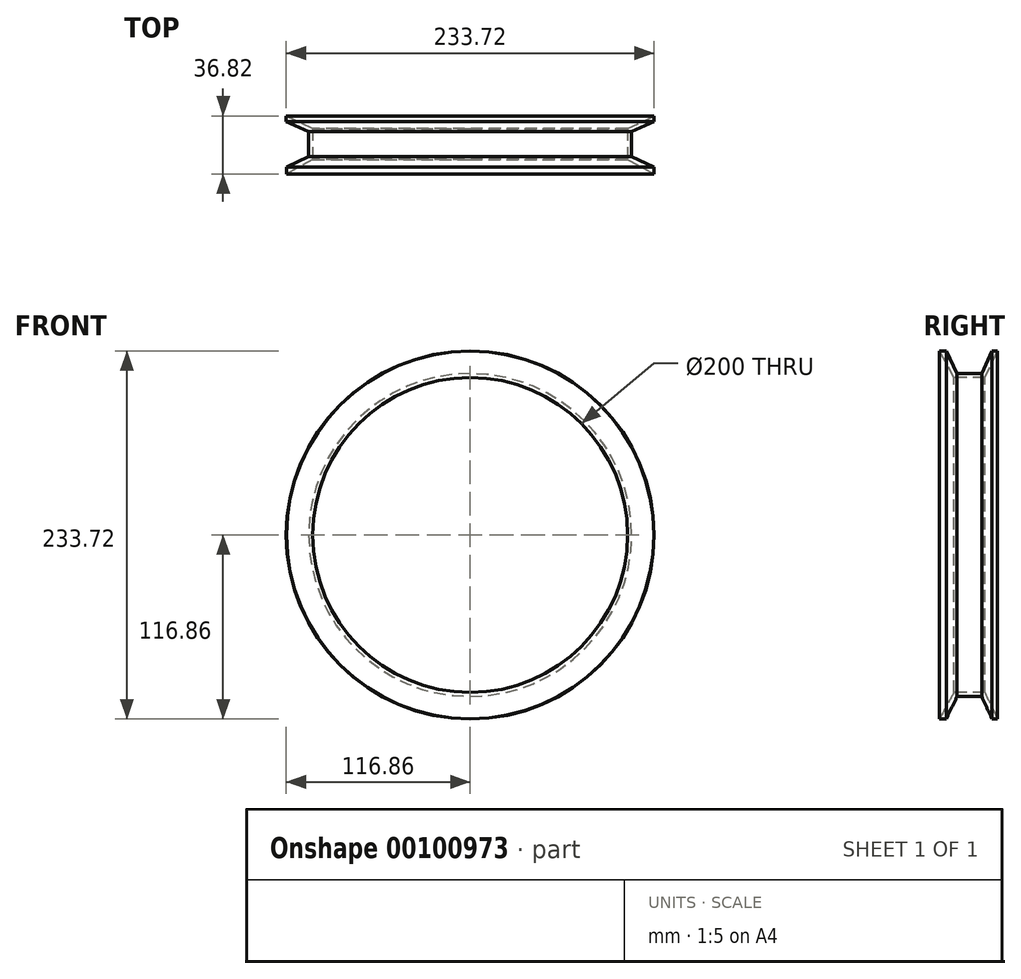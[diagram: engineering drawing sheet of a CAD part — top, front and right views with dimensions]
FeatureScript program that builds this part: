
annotation { "Feature Type Name" : "Feature", "Feature Type Description" : "" }
export const myFeature = defineFeature(function(context is Context, id is Id, definition is map)
    precondition{}
    {
        {
            var Q0;
            Q0=qCreatedBy(makeId("Right.planeOp"),FACE);
            var sketch = newSketch(context, id + "F0", { "sketchPlane" : qUnion([Q0])});
            skLineSegment(sketch, "E0", {"start": v(-18.41, 116.7) * mm, "end": v(-9.33, 100) * mm});
            skLineSegment(sketch, "E1", {"start": v(-9.33, 100) * mm, "end": v(10.28, 100) * mm});
            skLineSegment(sketch, "E2", {"start": v(10.28, 100) * mm, "end": v(18.41, 116.86) * mm});
            skLineSegment(sketch, "E3", {"start": v(18.41, 116.86) * mm, "end": v(14.86, 116.86) * mm});
            skLineSegment(sketch, "E4", {"start": v(14.86, 116.86) * mm, "end": v(8.34, 102.56) * mm});
            skLineSegment(sketch, "E5", {"start": v(8.34, 102.56) * mm, "end": v(-7.33, 102.56) * mm});
            skLineSegment(sketch, "E6", {"start": v(-7.33, 102.56) * mm, "end": v(-14.2, 116.74) * mm});
            skLineSegment(sketch, "E7", {"start": v(-14.2, 116.74) * mm, "end": v(-18.41, 116.7) * mm});
            skSolve(sketch);
        }
        {
            var Q0;
            Q0=qCreatedBy(makeId("Right.planeOp"),FACE);
            var sketch = newSketch(context, id + "F1", { "sketchPlane" : qUnion([Q0])});
            skLineSegment(sketch, "E8", {"start": v(0, 0) * mm, "end": v(66.3, 0) * mm});
            skSolve(sketch);
        }
        {
            var Q0;
            Q0=makeQuery(id+"F0.imprint","IMPRINT",FACE,{"disambiguationData":[TD([[makeQuery(id+"F0.imprint","IMPRINT",EDGE,{"derivedFrom":sQuery(id+"F0.wireOp",EDGE,"E0")}),1.0]])]});
            var Q1;
            Q1=sQuery(id+"F1.wireOp",EDGE,"E8");
            revolve(context, id + "F2", {"entities" : qUnion([Q0]), "axis" : qUnion([Q1]), "revolveType" : RevolveType.FULL});
        }
    });
